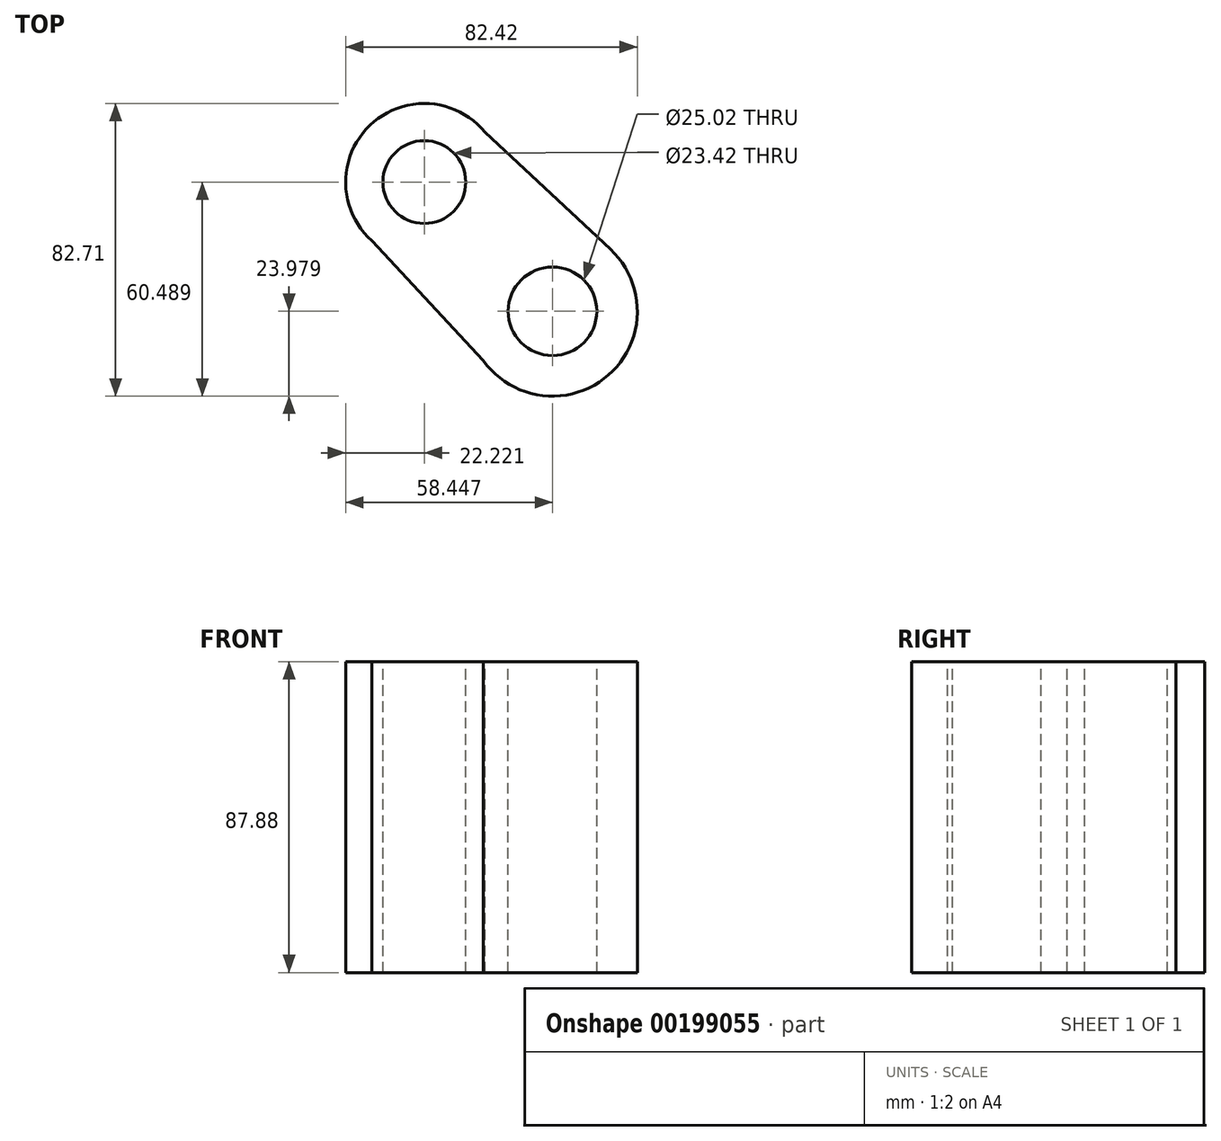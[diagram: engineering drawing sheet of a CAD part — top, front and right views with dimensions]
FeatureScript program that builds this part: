
annotation { "Feature Type Name" : "Feature", "Feature Type Description" : "" }
export const myFeature = defineFeature(function(context is Context, id is Id, definition is map)
    precondition{}
    {
        {
            var Q0;
            Q0=qCreatedBy(makeId("Top.planeOp"),FACE);
            var sketch = newSketch(context, id + "F0", { "sketchPlane" : qUnion([Q0])});
            skCircle(sketch, "E0", {"center": v(-45.64, 49.49) * mm, "radius": 22.22 * mm});
            skCircle(sketch, "E1", {"center": v(-45.64, 49.49) * mm, "radius": 11.7 * mm});
            skCircle(sketch, "E2", {"center": v(-9.41, 12.98) * mm, "radius": 23.98 * mm});
            skCircle(sketch, "E3", {"center": v(-9.41, 12.98) * mm, "radius": 12.51 * mm});
            skLineSegment(sketch, "E4", {"start": v(-63.2, 35.89) * mm, "end": v(-24.7, -5.5) * mm});
            skLineSegment(sketch, "E5", {"start": v(-28.46, 63.58) * mm, "end": v(6.95, 30.5) * mm});
            skSolve(sketch);
        }
        {
            var Q0;
            Q0 = qSketchRegion(id + "F0", true);
            extrude(context, id + "F1", {"entities" : qUnion([Q0]), "oppositeDirection" : true, "depth" : 87.88 * mm});
        }
    });
